# Revit family: Hekatron_Feststellanlagen_RSZ Kompakt Set ws_DE_22.01
name_source: partatom
category: Brandmelder
revit_build: Autodesk Revit 2018 (Build: 20190510_1515(x64)
units: mm (PartAtom-declared; Revit-internal decimal feet)

## family parameters
Basisbauteil = Fläche
Beim Laden mit Abzugskörper schneiden = Nein
Bemaßung runder Anschluss = Durchmesser verwenden
Beschriftungsausrichtung beibehalten = Ja
Gemeinsam genutzt = Nein
OmniClass-Nummer = 23.85.30.21
OmniClass-Titel = Environmental Detection/Registration
Raumberechnungspunkt = Nein
Teiletyp = Normal

## types (1)
- RSZ Compact Set ws
    Bauartgenehmigungen = Z-6.500-2393
    Beschreibung = Die RSZ Kompakt ist eine Rauchschaltzentrale in kompakter Bauform mit integriertem Sturzrauchschalter für den Einsatz an Brand- und Rauchschutztüren. Durch die kompakte Bauform und ihr variables Design ist sie speziell für die Kombination mit Türschließern mit integrierter Feststellung geeignet. Die RSZ Kompakt kann direkt auf dem Türrahmen neben- oder gegenüber dem Türschließer montiert werden. Zum Einsatz kommt sie in Feststellanlagen in den verschiedenen Anwendungen in Industrie- und Verwaltungsgebäuden.
    Betriebsspannung = 230 V AC
    Breite (mm) = 250.0
    Farbe = weiß, ähnlich RAL 9016
    Hersteller = Hekatron
    Höhe (mm) = 46.0
    Kabeleinführung = hinten, seitlich
    Link zu Ausschreibungstext = https://www.meinhplus.de
    Link zu Produktinformation = https://www.hekatron-planungstools.de
    Link zu ausschreiben.de = http://www.ausschreiben.de
    Link zum Datenblatt = https://www.hekatron-planungstools.de
    Material = PC
    Modell = RSZ Kompakt Set ws
    Montageart = Wand- oder Sturzmontage
    Schutzart = IP 40
    Tiefe (mm) = 36.0
    Typenkommentare = Rauchschalter-Zentrale Kompakt Set weiß
    UB A&S Artikel Nummer = 31-5300001-01-01
    URL = https://www.hekatron-brandschutz.de
    Version des BIM Objektes = 22.01
    Vorgabe-Ansicht = 1200 mm
    Zulässige Umgebungstemperatur = -20 °C bis +45 °C

## geometry (parser evidence)
native form markers: Extrusion x1, Sweep x2
no freeform markers — native parametric forms only
